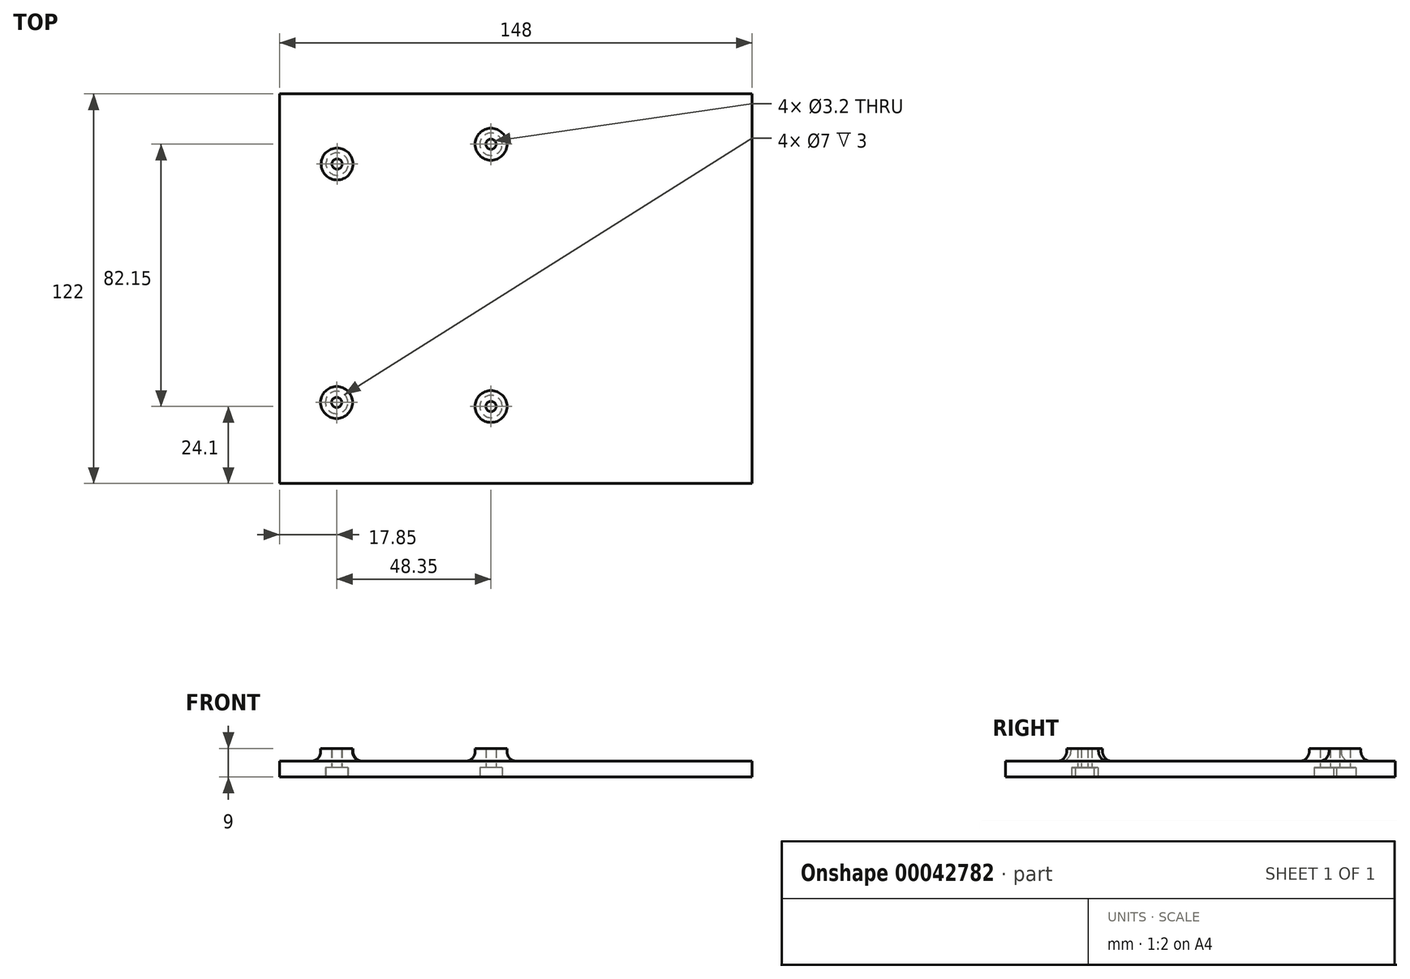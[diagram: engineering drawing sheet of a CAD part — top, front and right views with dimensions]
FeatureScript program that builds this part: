
annotation { "Feature Type Name" : "Feature", "Feature Type Description" : "" }
export const myFeature = defineFeature(function(context is Context, id is Id, definition is map)
    precondition{}
    {
        {
            var Q0;
            Q0=qCreatedBy(makeId("Top.planeOp"),FACE);
            var sketch = newSketch(context, id + "F0", { "sketchPlane" : qUnion([Q0])});
            skLineSegment(sketch, "E0.rect.bottom", {"start": v(32, -51) * mm, "end": v(-32, -51) * mm});
            skLineSegment(sketch, "E0.rect.top", {"start": v(32, 51) * mm, "end": v(-32, 51) * mm});
            skLineSegment(sketch, "E0.rect.left", {"start": v(32, -51) * mm, "end": v(32, 51) * mm});
            skLineSegment(sketch, "E0.rect.right", {"start": v(-32, -51) * mm, "end": v(-32, 51) * mm});
            skPoint(sketch, "E0.rect.middle", {"position": v(0, 0) * mm});
            skCircle(sketch, "E1", {"center": v(-24, 39.05) * mm, "radius": 1.6 * mm});
            skCircle(sketch, "E2", {"center": v(24.2, 45.25) * mm, "radius": 1.6 * mm});
            skCircle(sketch, "E3", {"center": v(24.2, -36.9) * mm, "radius": 1.6 * mm});
            skCircle(sketch, "E4", {"center": v(-24.15, -35.65) * mm, "radius": 1.6 * mm});
            skLineSegment(sketch, "E5.rect.bottom", {"start": v(96, -41) * mm, "end": v(42, -41) * mm});
            skLineSegment(sketch, "E5.rect.top", {"start": v(96, 41) * mm, "end": v(42, 41) * mm});
            skLineSegment(sketch, "E5.rect.left", {"start": v(96, -41) * mm, "end": v(96, 41) * mm});
            skLineSegment(sketch, "E5.rect.right", {"start": v(42, -41) * mm, "end": v(42, 41) * mm});
            skPoint(sketch, "E5.rect.middle", {"position": v(69, 0) * mm});
            skLineSegment(sketch, "E6.bottom", {"start": v(-42, 61) * mm, "end": v(106, 61) * mm});
            skLineSegment(sketch, "E6.top", {"start": v(-42, -61) * mm, "end": v(106, -61) * mm});
            skLineSegment(sketch, "E6.left", {"start": v(-42, 61) * mm, "end": v(-42, -61) * mm});
            skLineSegment(sketch, "E6.right", {"start": v(106, 61) * mm, "end": v(106, -61) * mm});
            skCircle(sketch, "E7", {"center": v(-24.15, -35.65) * mm, "radius": 5 * mm});
            skCircle(sketch, "E8", {"center": v(24.2, -36.9) * mm, "radius": 5 * mm});
            skCircle(sketch, "E9", {"center": v(24.2, 45.25) * mm, "radius": 5 * mm});
            skCircle(sketch, "E10", {"center": v(-24, 39.05) * mm, "radius": 5 * mm});
            skCircle(sketch, "E11", {"center": v(24.2, -36.9) * mm, "radius": 3.5 * mm});
            skCircle(sketch, "E12", {"center": v(-24.15, -35.65) * mm, "radius": 3.5 * mm});
            skCircle(sketch, "E13", {"center": v(-24, 39.05) * mm, "radius": 3.5 * mm});
            skCircle(sketch, "E14", {"center": v(24.2, 45.25) * mm, "radius": 3.5 * mm});
            skSolve(sketch);
        }
        {
            var Q0;
            Q0=makeQuery(id+"F0.imprint","IMPRINT",FACE,{"disambiguationData":[TD([[makeQuery(id+"F0.imprint","IMPRINT",EDGE,{"derivedFrom":sQuery(id+"F0.wireOp",EDGE,"E5.rect.bottom")}),-1.0]])]});
            var Q1;
            Q1=makeQuery(id+"F0.imprint","IMPRINT",FACE,{"disambiguationData":[TD([[makeQuery(id+"F0.imprint","IMPRINT",EDGE,{"derivedFrom":sQuery(id+"F0.wireOp",EDGE,"E0.rect.bottom")}),1.0]])]});
            var Q2;
            Q2=makeQuery(id+"F0.imprint","IMPRINT",FACE,{"disambiguationData":[TD([[makeQuery(id+"F0.imprint","IMPRINT",EDGE,{"derivedFrom":sQuery(id+"F0.wireOp",EDGE,"E0.rect.bottom")}),-1.0]])]});
            var Q3;
            Q3=makeQuery(id+"F0.imprint","IMPRINT",FACE,{"disambiguationData":[TD([[makeQuery(id+"F0.imprint","IMPRINT",EDGE,{"derivedFrom":sQuery(id+"F0.wireOp",EDGE,"E4")}),-1.0]])]});
            var Q4;
            Q4=makeQuery(id+"F0.imprint","IMPRINT",FACE,{"disambiguationData":[TD([[makeQuery(id+"F0.imprint","IMPRINT",EDGE,{"derivedFrom":sQuery(id+"F0.wireOp",EDGE,"E3")}),-1.0]])]});
            var Q5;
            Q5=makeQuery(id+"F0.imprint","IMPRINT",FACE,{"disambiguationData":[TD([[makeQuery(id+"F0.imprint","IMPRINT",EDGE,{"derivedFrom":sQuery(id+"F0.wireOp",EDGE,"E2")}),-1.0]])]});
            var Q6;
            Q6=makeQuery(id+"F0.imprint","IMPRINT",FACE,{"disambiguationData":[TD([[makeQuery(id+"F0.imprint","IMPRINT",EDGE,{"derivedFrom":sQuery(id+"F0.wireOp",EDGE,"E1")}),-1.0]])]});
            var Q7;
            Q7=makeQuery(id+"F0.imprint","IMPRINT",FACE,{"disambiguationData":[TD([[makeQuery(id+"F0.imprint","IMPRINT",EDGE,{"derivedFrom":sQuery(id+"F0.wireOp",EDGE,"E8")}),1.0]])]});
            var Q8;
            Q8=makeQuery(id+"F0.imprint","IMPRINT",FACE,{"disambiguationData":[TD([[makeQuery(id+"F0.imprint","IMPRINT",EDGE,{"derivedFrom":sQuery(id+"F0.wireOp",EDGE,"E7")}),1.0]])]});
            var Q9;
            Q9=makeQuery(id+"F0.imprint","IMPRINT",FACE,{"disambiguationData":[TD([[makeQuery(id+"F0.imprint","IMPRINT",EDGE,{"derivedFrom":sQuery(id+"F0.wireOp",EDGE,"E10")}),1.0]])]});
            var Q10;
            Q10=makeQuery(id+"F0.imprint","IMPRINT",FACE,{"disambiguationData":[TD([[makeQuery(id+"F0.imprint","IMPRINT",EDGE,{"derivedFrom":sQuery(id+"F0.wireOp",EDGE,"E9")}),1.0]])]});
            extrude(context, id + "F1", {"entities" : qUnion([Q0, Q1, Q2, Q3, Q4, Q5, Q6, Q7, Q8, Q9, Q10]), "depth" : 5 * mm});
        }
        {
            var Q0;
            Q0=makeQuery(id+"F0.imprint","IMPRINT",FACE,{"disambiguationData":[TD([[makeQuery(id+"F0.imprint","IMPRINT",EDGE,{"derivedFrom":sQuery(id+"F0.wireOp",EDGE,"E1")}),-1.0]])]});
            var Q1;
            Q1=makeQuery(id+"F0.imprint","IMPRINT",FACE,{"disambiguationData":[TD([[makeQuery(id+"F0.imprint","IMPRINT",EDGE,{"derivedFrom":sQuery(id+"F0.wireOp",EDGE,"E2")}),-1.0]])]});
            var Q2;
            Q2=makeQuery(id+"F0.imprint","IMPRINT",FACE,{"disambiguationData":[TD([[makeQuery(id+"F0.imprint","IMPRINT",EDGE,{"derivedFrom":sQuery(id+"F0.wireOp",EDGE,"E3")}),-1.0]])]});
            var Q3;
            Q3=makeQuery(id+"F0.imprint","IMPRINT",FACE,{"disambiguationData":[TD([[makeQuery(id+"F0.imprint","IMPRINT",EDGE,{"derivedFrom":sQuery(id+"F0.wireOp",EDGE,"E4")}),-1.0]])]});
            var Q4;
            Q4=makeQuery(id+"F0.imprint","IMPRINT",FACE,{"disambiguationData":[TD([[makeQuery(id+"F0.imprint","IMPRINT",EDGE,{"derivedFrom":sQuery(id+"F0.wireOp",EDGE,"E8")}),1.0]])]});
            var Q5;
            Q5=makeQuery(id+"F0.imprint","IMPRINT",FACE,{"disambiguationData":[TD([[makeQuery(id+"F0.imprint","IMPRINT",EDGE,{"derivedFrom":sQuery(id+"F0.wireOp",EDGE,"E7")}),1.0]])]});
            var Q6;
            Q6=makeQuery(id+"F0.imprint","IMPRINT",FACE,{"disambiguationData":[TD([[makeQuery(id+"F0.imprint","IMPRINT",EDGE,{"derivedFrom":sQuery(id+"F0.wireOp",EDGE,"E10")}),1.0]])]});
            var Q7;
            Q7=makeQuery(id+"F0.imprint","IMPRINT",FACE,{"disambiguationData":[TD([[makeQuery(id+"F0.imprint","IMPRINT",EDGE,{"derivedFrom":sQuery(id+"F0.wireOp",EDGE,"E9")}),1.0]])]});
            extrude(context, id + "F2", {"entities" : qUnion([Q0, Q1, Q2, Q3, Q4, Q5, Q6, Q7]), "operationType" : NewBodyOperationType.ADD, "depth" : 9 * mm});
        }
        {
            var Q0;
            Q0=makeQuery(id+"F0.imprint","IMPRINT",FACE,{"disambiguationData":[TD([[makeQuery(id+"F0.imprint","IMPRINT",EDGE,{"derivedFrom":sQuery(id+"F0.wireOp",EDGE,"E3")}),-1.0]])]});
            var Q1;
            Q1=makeQuery(id+"F0.imprint","IMPRINT",FACE,{"disambiguationData":[TD([[makeQuery(id+"F0.imprint","IMPRINT",EDGE,{"derivedFrom":sQuery(id+"F0.wireOp",EDGE,"E4")}),-1.0]])]});
            var Q2;
            Q2=makeQuery(id+"F0.imprint","IMPRINT",FACE,{"disambiguationData":[TD([[makeQuery(id+"F0.imprint","IMPRINT",EDGE,{"derivedFrom":sQuery(id+"F0.wireOp",EDGE,"E1")}),-1.0]])]});
            var Q3;
            Q3=makeQuery(id+"F0.imprint","IMPRINT",FACE,{"disambiguationData":[TD([[makeQuery(id+"F0.imprint","IMPRINT",EDGE,{"derivedFrom":sQuery(id+"F0.wireOp",EDGE,"E2")}),-1.0]])]});
            extrude(context, id + "F3", {"entities" : qUnion([Q0, Q1, Q2, Q3]), "operationType" : NewBodyOperationType.REMOVE, "depth" : 3 * mm});
        }
        {
            var Q0;
            Q0=makeQuery(id+"F2.boolean.opBoolean","INTERSECT",EDGE,{"derivedFrom":[makeQuery(id+"F1.opExtrude","CAP_FACE",FACE,{"disambiguationData":[OSD([sQuery(id+"F0.wireOp",EDGE,"E1"),sQuery(id+"F0.wireOp",EDGE,"E2"),sQuery(id+"F0.wireOp",EDGE,"E3"),sQuery(id+"F0.wireOp",EDGE,"E4"),sQuery(id+"F0.wireOp",EDGE,"E6.bottom"),sQuery(id+"F0.wireOp",EDGE,"E6.top"),sQuery(id+"F0.wireOp",EDGE,"E6.left"),sQuery(id+"F0.wireOp",EDGE,"E6.right")])],"isStart":false}),makeQuery(id+"F2.opExtrude","SWEPT_FACE",FACE,{"disambiguationData":[OSD([sQuery(id+"F0.wireOp",EDGE,"E8")])]})]});
            var Q1;
            Q1=makeQuery(id+"F2.boolean.opBoolean","INTERSECT",EDGE,{"derivedFrom":[makeQuery(id+"F1.opExtrude","CAP_FACE",FACE,{"disambiguationData":[OSD([sQuery(id+"F0.wireOp",EDGE,"E1"),sQuery(id+"F0.wireOp",EDGE,"E2"),sQuery(id+"F0.wireOp",EDGE,"E3"),sQuery(id+"F0.wireOp",EDGE,"E4"),sQuery(id+"F0.wireOp",EDGE,"E6.bottom"),sQuery(id+"F0.wireOp",EDGE,"E6.top"),sQuery(id+"F0.wireOp",EDGE,"E6.left"),sQuery(id+"F0.wireOp",EDGE,"E6.right")])],"isStart":false}),makeQuery(id+"F2.opExtrude","SWEPT_FACE",FACE,{"disambiguationData":[OSD([sQuery(id+"F0.wireOp",EDGE,"E9")])]})]});
            var Q2;
            Q2=makeQuery(id+"F2.boolean.opBoolean","INTERSECT",EDGE,{"derivedFrom":[makeQuery(id+"F1.opExtrude","CAP_FACE",FACE,{"disambiguationData":[OSD([sQuery(id+"F0.wireOp",EDGE,"E1"),sQuery(id+"F0.wireOp",EDGE,"E2"),sQuery(id+"F0.wireOp",EDGE,"E3"),sQuery(id+"F0.wireOp",EDGE,"E4"),sQuery(id+"F0.wireOp",EDGE,"E6.bottom"),sQuery(id+"F0.wireOp",EDGE,"E6.top"),sQuery(id+"F0.wireOp",EDGE,"E6.left"),sQuery(id+"F0.wireOp",EDGE,"E6.right")])],"isStart":false}),makeQuery(id+"F2.opExtrude","SWEPT_FACE",FACE,{"disambiguationData":[OSD([sQuery(id+"F0.wireOp",EDGE,"E7")])]})]});
            var Q3;
            Q3=makeQuery(id+"F2.boolean.opBoolean","INTERSECT",EDGE,{"derivedFrom":[makeQuery(id+"F1.opExtrude","CAP_FACE",FACE,{"disambiguationData":[OSD([sQuery(id+"F0.wireOp",EDGE,"E1"),sQuery(id+"F0.wireOp",EDGE,"E2"),sQuery(id+"F0.wireOp",EDGE,"E3"),sQuery(id+"F0.wireOp",EDGE,"E4"),sQuery(id+"F0.wireOp",EDGE,"E6.bottom"),sQuery(id+"F0.wireOp",EDGE,"E6.top"),sQuery(id+"F0.wireOp",EDGE,"E6.left"),sQuery(id+"F0.wireOp",EDGE,"E6.right")])],"isStart":false}),makeQuery(id+"F2.opExtrude","SWEPT_FACE",FACE,{"disambiguationData":[OSD([sQuery(id+"F0.wireOp",EDGE,"E10")])]})]});
            fillet(context, id + "F4", {"entities" : qUnion([Q0, Q1, Q2, Q3]), "radius" : 3 * mm, "tangentPropagation" : true, "allowEdgeOverflow" : false});
        }
    });
